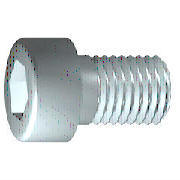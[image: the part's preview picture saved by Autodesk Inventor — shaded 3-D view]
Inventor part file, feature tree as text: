
AUTODESK INVENTOR PART (.ipt)
format: ipt  version: 2022 (Build 260153000, 153)  size: 194,048 bytes
history: native  units: mm (DEFAULTED — no unit token found)
features: sketch x2, other x1, extrude x1, plane x1, fillet x1
ambient origin geometry x7: Origin, YZ Plane, XY Plane, X Axis, Y Axis, Z Axis, Center Point
bodies: Solid1 (feature_tree)
feature tree (6):
  other  "Базовый элемент"
  extrude  "Паз"  Depth=17.6mm
  plane  "Work Plane1"
  fillet  "Fillet2"  Radius=0.49086mm
  sketch  "Эскиз1"
  sketch  "Эскиз2"
